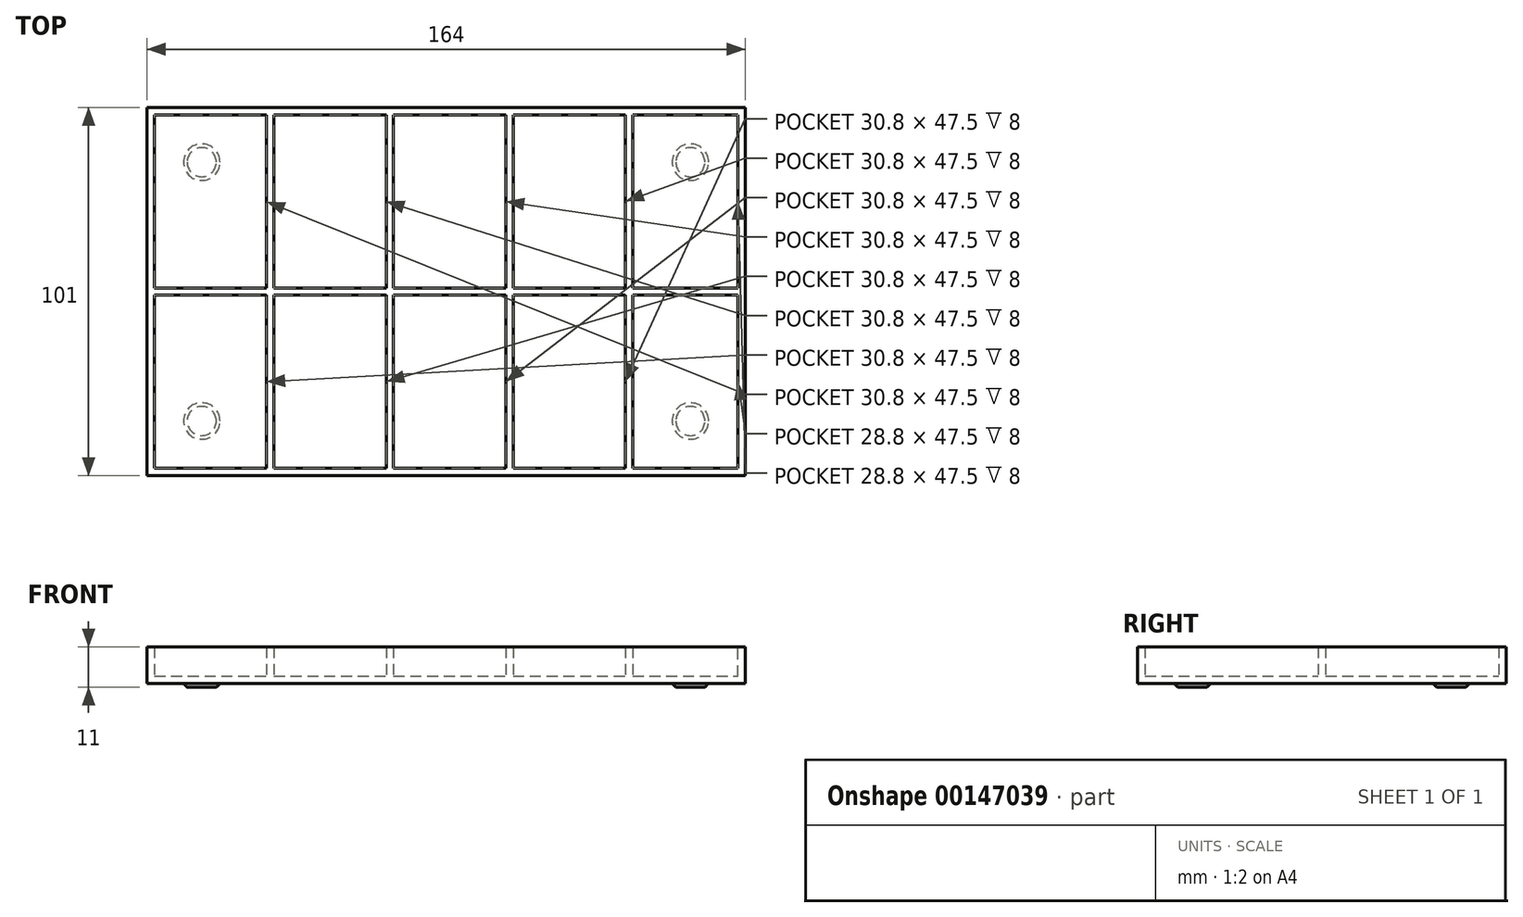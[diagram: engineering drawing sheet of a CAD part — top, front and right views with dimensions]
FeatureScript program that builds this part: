
annotation { "Feature Type Name" : "Feature", "Feature Type Description" : "" }
export const myFeature = defineFeature(function(context is Context, id is Id, definition is map)
    precondition{}
    {
        {
            var Q0;
            Q0=qCreatedBy(makeId("Top.planeOp"),FACE);
            var sketch = newSketch(context, id + "F0", { "sketchPlane" : qUnion([Q0])});
            skLineSegment(sketch, "E0.bottom", {"start": v(-82, -50.5) * mm, "end": v(82, -50.5) * mm});
            skLineSegment(sketch, "E0.top", {"start": v(-82, 50.5) * mm, "end": v(82, 50.5) * mm});
            skLineSegment(sketch, "E0.left", {"start": v(-82, -50.5) * mm, "end": v(-82, 50.5) * mm});
            skLineSegment(sketch, "E0.right", {"start": v(82, -50.5) * mm, "end": v(82, 50.5) * mm});
            skPoint(sketch, "E0.middle", {"position": v(0, 0) * mm});
            skSolve(sketch);
        }
        {
            var Q0;
            Q0 = qSketchRegion(id + "F0", true);
            extrude(context, id + "F1", {"entities" : qUnion([Q0]), "depth" : 10 * mm});
        }
        {
            var Q0;
            Q0=makeQuery(id+"F1.opExtrude","CAP_FACE",FACE,{"disambiguationData":[OSD([sQuery(id+"F0.wireOp",EDGE,"E0.bottom"),sQuery(id+"F0.wireOp",EDGE,"E0.top"),sQuery(id+"F0.wireOp",EDGE,"E0.left"),sQuery(id+"F0.wireOp",EDGE,"E0.right")])],"isStart":false});
            var sketch = newSketch(context, id + "F2", { "sketchPlane" : qUnion([Q0])});
            skLineSegment(sketch, "E1.bottom", {"start": v(-80, -48.5) * mm, "end": v(80, -48.5) * mm});
            skLineSegment(sketch, "E1.top", {"start": v(-80, 48.5) * mm, "end": v(80, 48.5) * mm});
            skLineSegment(sketch, "E1.left", {"start": v(-80, -48.5) * mm, "end": v(-80, 48.5) * mm});
            skLineSegment(sketch, "E1.right", {"start": v(80, -48.5) * mm, "end": v(80, 48.5) * mm});
            skPoint(sketch, "E1.middle", {"position": v(0, 0) * mm});
            skSolve(sketch);
        }
        {
            var Q0;
            Q0 = qSketchRegion(id + "F2", true);
            extrude(context, id + "F3", {"entities" : qUnion([Q0]), "operationType" : NewBodyOperationType.REMOVE, "oppositeDirection" : true, "depth" : 8 * mm});
        }
        {
            var Q0;
            Q0=makeQuery(id+"F3.boolean.opBoolean","COPY",FACE,{"derivedFrom":makeQuery(id+"F3.opExtrude","CAP_FACE",FACE,{"disambiguationData":[OSD([sQuery(id+"F2.wireOp",EDGE,"E1.bottom"),sQuery(id+"F2.wireOp",EDGE,"E1.top"),sQuery(id+"F2.wireOp",EDGE,"E1.left"),sQuery(id+"F2.wireOp",EDGE,"E1.right")])],"isStart":false})});
            var sketch = newSketch(context, id + "F4", { "sketchPlane" : qUnion([Q0])});
            skLineSegment(sketch, "E2.bottom", {"start": v(80, 1) * mm, "end": v(-80, 1) * mm});
            skLineSegment(sketch, "E2.top", {"start": v(80, -1) * mm, "end": v(-80, -1) * mm});
            skLineSegment(sketch, "E2.left", {"start": v(80, 1) * mm, "end": v(80, -1) * mm});
            skLineSegment(sketch, "E2.right", {"start": v(-80, 1) * mm, "end": v(-80, -1) * mm});
            skPoint(sketch, "E2.middle", {"position": v(0, 0) * mm});
            skSolve(sketch);
        }
        {
            var Q0;
            Q0 = qSketchRegion(id + "F4", true);
            extrude(context, id + "F5", {"entities" : qUnion([Q0]), "operationType" : NewBodyOperationType.ADD, "depth" : 8 * mm});
        }
        {
            var Q0;
            {var subQ0=sQuery(id+"F2.wireOp",EDGE,"E1.bottom");var subQ1=sQuery(id+"F2.wireOp",EDGE,"E1.left");var subQ2=sQuery(id+"F2.wireOp",EDGE,"E1.right");Q0=makeQuery(id+"F5.boolean.opBoolean","SPLIT",FACE,{"disambiguationData":[TD([makeQuery(id+"F3.boolean.opBoolean","COPY",FACE,{"derivedFrom":makeQuery(id+"F3.opExtrude","SWEPT_FACE",FACE,{"disambiguationData":[OSD([subQ0])]})})])],"derivedFrom":makeQuery(id+"F3.boolean.opBoolean","COPY",FACE,{"derivedFrom":makeQuery(id+"F3.opExtrude","CAP_FACE",FACE,{"disambiguationData":[OSD([subQ0,sQuery(id+"F2.wireOp",EDGE,"E1.top"),subQ1,subQ2])],"isStart":false})})});}
            var sketch = newSketch(context, id + "F6", { "sketchPlane" : qUnion([Q0])});
            skLineSegment(sketch, "E3.bottom", {"start": v(-49.2, -48.5) * mm, "end": v(-47.2, -48.5) * mm});
            skLineSegment(sketch, "E3.top", {"start": v(-49.2, 48.5) * mm, "end": v(-47.2, 48.5) * mm});
            skLineSegment(sketch, "E3.left", {"start": v(-49.2, -48.5) * mm, "end": v(-49.2, 48.5) * mm});
            skLineSegment(sketch, "E3.right", {"start": v(-47.2, -48.5) * mm, "end": v(-47.2, 48.5) * mm});
            skLineSegment(sketch, "E4.bottom", {"start": v(-16.4, -48.5) * mm, "end": v(-14.4, -48.5) * mm});
            skLineSegment(sketch, "E4.top", {"start": v(-16.4, 48.5) * mm, "end": v(-14.4, 48.5) * mm});
            skLineSegment(sketch, "E4.left", {"start": v(-16.4, -48.5) * mm, "end": v(-16.4, 48.5) * mm});
            skLineSegment(sketch, "E4.right", {"start": v(-14.4, -48.5) * mm, "end": v(-14.4, 48.5) * mm});
            skLineSegment(sketch, "E5.bottom", {"start": v(18.4, -48.5) * mm, "end": v(16.4, -48.5) * mm});
            skLineSegment(sketch, "E5.top", {"start": v(18.4, 48.5) * mm, "end": v(16.4, 48.5) * mm});
            skLineSegment(sketch, "E5.left", {"start": v(18.4, -48.5) * mm, "end": v(18.4, 48.5) * mm});
            skLineSegment(sketch, "E5.right", {"start": v(16.4, -48.5) * mm, "end": v(16.4, 48.5) * mm});
            skLineSegment(sketch, "E6.bottom", {"start": v(49.2, -48.5) * mm, "end": v(51.2, -48.5) * mm});
            skLineSegment(sketch, "E6.top", {"start": v(49.2, 48.5) * mm, "end": v(51.2, 48.5) * mm});
            skLineSegment(sketch, "E6.left", {"start": v(49.2, -48.5) * mm, "end": v(49.2, 48.5) * mm});
            skLineSegment(sketch, "E6.right", {"start": v(51.2, -48.5) * mm, "end": v(51.2, 48.5) * mm});
            skSolve(sketch);
        }
        {
            var Q0;
            Q0 = qSketchRegion(id + "F6", true);
            extrude(context, id + "F7", {"entities" : qUnion([Q0]), "operationType" : NewBodyOperationType.ADD, "depth" : 8 * mm});
        }
        {
            var Q0;
            Q0=makeQuery(id+"F1.opExtrude","CAP_FACE",FACE,{"disambiguationData":[OSD([sQuery(id+"F0.wireOp",EDGE,"E0.bottom"),sQuery(id+"F0.wireOp",EDGE,"E0.top"),sQuery(id+"F0.wireOp",EDGE,"E0.left"),sQuery(id+"F0.wireOp",EDGE,"E0.right")])],"isStart":true});
            var sketch = newSketch(context, id + "F8", { "sketchPlane" : qUnion([Q0])});
            skCircle(sketch, "E7", {"center": v(-67, 35.5) * mm, "radius": 5 * mm});
            skCircle(sketch, "E8", {"center": v(67, 35.5) * mm, "radius": 5 * mm});
            skCircle(sketch, "E9", {"center": v(67, -35.5) * mm, "radius": 5 * mm});
            skCircle(sketch, "E10", {"center": v(-67, -35.5) * mm, "radius": 5 * mm});
            skSolve(sketch);
        }
        {
            var Q0;
            Q0 = qSketchRegion(id + "F8", true);
            extrude(context, id + "F9", {"entities" : qUnion([Q0]), "operationType" : NewBodyOperationType.ADD, "depth" : 1 * mm});
        }
        {
            var Q0;
            Q0=makeQuery(id+"F9.opExtrude","CAP_EDGE",EDGE,{"disambiguationData":[OSD([sQuery(id+"F8.wireOp",EDGE,"E7")])],"isStart":false});
            var Q1;
            Q1=makeQuery(id+"F9.opExtrude","CAP_EDGE",EDGE,{"disambiguationData":[OSD([sQuery(id+"F8.wireOp",EDGE,"E10")])],"isStart":false});
            var Q2;
            Q2=makeQuery(id+"F9.opExtrude","CAP_EDGE",EDGE,{"disambiguationData":[OSD([sQuery(id+"F8.wireOp",EDGE,"E8")])],"isStart":false});
            var Q3;
            Q3=makeQuery(id+"F9.opExtrude","CAP_EDGE",EDGE,{"disambiguationData":[OSD([sQuery(id+"F8.wireOp",EDGE,"E9")])],"isStart":false});
            chamfer(context, id + "F10", {"entities" : qUnion([Q0, Q1, Q2, Q3]), "width" : 1 * mm, "tangentPropagation" : true});
        }
    });
